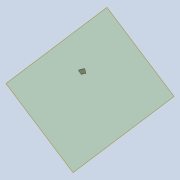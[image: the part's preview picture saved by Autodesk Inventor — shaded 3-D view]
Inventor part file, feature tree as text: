
AUTODESK INVENTOR PART (.ipt)
format: ipt  version: 2020 (Build 240168000, 168)  size: 9,062,912 bytes
history: native  units: in
note: dims shown in document units (in); Inventor stores cm internally (conversion verified against a paired STEP export)
features: other x165, extrude x70, fillet x51, projected_geometry x6, sketch x5, move_body x5, hole x4, loft x3, boolean_combine x2, plane x2, reference x2, direct_edit x1, split x1
ambient origin geometry x8: Origin, YZ Plane, XZ Plane, XY Plane, X Axis, Y Axis, Z Axis, Center Point
bodies: Body (feature_tree), BodyFeature (feature_tree), BodyCut (feature_tree), BodyCutFeature (feature_tree), BodyCutFilletFeature (feature_tree), BodyCutCombineFeature (feature_tree), BodyCutEdgeFilletFeature (feature_tree), BodyRibFrontFilletsFeature (feature_tree), BodyBackRibFilletsFeature (feature_tree), BodyFretboardFilletsFeature (feature_tree), BodyFrontTopFilletsFeature (feature_tree), BodyFrontBottomFilletsFeature (feature_tree), BodyFrontNeckFilletsFeature (feature_tree), Solid22 (feature_tree), Solid23 (feature_tree), Solid62 (feature_tree), Solid64 (feature_tree), Solid65 (feature_tree), Solid68 (feature_tree), Solid50 (feature_tree), Solid52 (feature_tree), Solid54 (feature_tree), Solid56 (feature_tree), Solid57 (feature_tree), Solid59 (feature_tree)
feature tree (317):
  other  "MainBody"
  extrude  "NeckMountsProfileFeature"  Depth=0.5in TaperAngle=0.0deg
  other  "NeckPlane"
  extrude  "8StringFeature"  Depth=4.5in
  extrude  "6StringFeature"  Depth=1.12in
  extrude  "HornFeature"  Depth=0.6788in
  other  "6StringNeckFeature"
  other  "8StringNeckFeature"
  fillet  "InsideCornerFilletsFeature1/8"  Radius=0.6788in
  fillet  "OutsideFilletsFeature1/2"  Radius=0.125in
  fillet  "NeckMountOutsideFilletsFeature1/4"  Radius=0.5in
  fillet  "TipFilletsFeature1/8"  Radius=0.125in
  fillet  "BottomHornTipFilletFeature1/10"  Radius=0.1in
  fillet  "BottomHornFilletsFeature1/8"  Radius=0.125in
  fillet  "InsideHandleFilletsFeature1/2"  Radius=0.5in
  fillet  "InsideHandleFilletsFeature1/8"  Radius=0.125in
  fillet  "InsideTopHornFilletsFeature1/4"  Radius=0.25in
  fillet  "InsideTopHornFilletsFeature1/2"  Radius=0.5in
  fillet  "InsideBottomHornFilletsFeature1/4"  Radius=0.25in
  other  "PickupsOriginal"
  other  "MiddlePlane"
  other  "PickupsCustom"
  other  "PickupsModified"
  extrude  "TopPickupsIndentFeature"  Depth=0.05in
  extrude  "BottomPickupsIndentFeature"  Depth=0.05in
  extrude  "TopPickupHolesFeature"  Depth=0.05in
  extrude  "BottomPickupHolesFeature"  Depth=0.05in
  fillet  "PickupIndentFilletsFeature"  Radius=1.1649in
  other  "Frets"
  other  "FretsPreview"
  other  "TopHornHandleIndent"
  extrude  "TopHornBodyHandleFeature"  Depth=0.05in
  extrude  "TopHornHornHandleFeature"  Depth=0.05in
  other  "HornSculptFeature"
  other  "TopHornHandleFront"
  extrude  "TopHornHandleFrontFeature"  Depth=0.05in
  extrude  "TopHornHandleFront2Feature"  Depth=0.05in
  extrude  "TopHornHandleFront3Feature"  TaperAngle=45.0deg  [1 undecoded]
  other  "TopHornHandleBack"
  extrude  "TopHornHandleBackFeature"  TaperAngle=120.0deg  [1 undecoded]
  extrude  "TopHornHandleBack2Feature"  Depth=0.05in
  extrude  "TopHandleFeature"  Depth=0.05in
  extrude  "TopHandleFrontFeature"  Depth=0.05in
  extrude  "TopHandleBackFeature"  Depth=0.05in
  other  "Tuners"
  hole  "TunerHolesFeature"  [1 undecoded]
  other  "LogoMount"
  extrude  "LogoMountFeature"  Depth=0.05in
  other  "SideProfile"
  extrude  "SideProfileFeature"  Depth=0.05in
  other  "KeyboardCompartmentSidePlane"
  extrude  "KeyboardCompartmentFeature"  Depth=0.05in
  fillet  "KeyboardCompartmentFilletsFeature"  Radius=0.101in
  other  "ControlsBottom"
  other  "ControlsTop2"
  other  "ControlsTop1"
  extrude  "ControlsTop1Feature"  Depth=0.05in
  extrude  "ControlsTop2Feature"  Depth=0.05in
  extrude  "ControlsBottomFeature"  Depth=0.05in
  other  "HornSculptSideProfileFeature"
  fillet  "HornFretboardFilletFeature"  Radius=0.933in
  other  "ElectronicsCompartments"
  other  "InsideFacePlane1"
  other  "InsideFacePlane2"
  other  "InsideFacePlane3"
  extrude  "ElectronicCompartmentTopFeature"  Depth=0.05in
  extrude  "ElectronicCompartmentBottomFeature"  Depth=0.05in
  other  "ElectronicCompartmentsSculpt1Feature"
  other  "ElectronicCompartmentsSculpt2Feature"
  other  "ElectronicCompartmentsSculpt3Feature"
  other  "ElectronicCompartmentsSubtractFeature"
  extrude  "ElectronicCompartmentsSubtract2Feature"  Depth=0.05in
  fillet  "ElectronicCompartmentFillets1Feature"  Radius=3.5in
  fillet  "ElectronicCompartmentFillets2Feature"  Radius=1.277in
  extrude  "ControlIndentsBottomFeature"  Depth=0.05in
  fillet  "ElectronicCompartmentFillets3Feature"  Radius=1.5in
  fillet  "ElectronicCompartmentFillets4Feature"  Radius=1.0857in
  extrude  "ControlIndentsTopFeature"  Depth=0.05in
  other  "ControlIndents2Top"
  extrude  "ControlIndents2TopFeature"  Depth=0.05in
  fillet  "ControlIndents3FilletsFeature"  Radius=4.5in
  extrude  "ControlIndents2RecutFeature"  Depth=0.05in
  fillet  "ElectronicCompartmentInsideFilletsFeature"  Radius=0.1512in
  other  "BottomBridgePickupWirePlane"
  extrude  "BottomBridgePickupWireHoleFeature"  Depth=0.05in
  other  "BottomNeckPickupWirePlane"
  extrude  "BottomNeckPickupWireFeature"  Depth=0.05in
  extrude  "TopPickupWireFeature"  Depth=0.05in
  other  "SeaboardBlockCircuitboardMounts"
  extrude  "SeaboardBlockMountStemFeature"  Depth=0.05in
  extrude  "SeaboardBlockMountsFeature"  Depth=0.05in
  other  "SeaboardBlockKeyMounts"
  extrude  "SeaboardBlockKeyMountsFeature"  Depth=0.05in
  extrude  "SeaboardBlockRibbonsFeature"  Depth=0.05in
  extrude  "TunersTopFeature"  Depth=0.05in
  extrude  "TunersMiddleFeature"  Depth=0.05in
  extrude  "TunersBottomFeature"  Depth=0.05in
  fillet  "TunerFilletsFeature"  Radius=1.1386in
  extrude  "NeckCutFeature"  Depth=0.05in
  fillet  "NeckCutFilletFeature"  Radius=4.009in
  other  "NeckCutCombineFeature"
  fillet  "NeckCutEdgeFilletFeature"  Radius=1.481in
  fillet  "NeckCutCornerFilletsFeature"  Radius=0.25in
  extrude  "NeckMountsFeature"  Depth=0.05in
  extrude  "FretMarkersTopFeature"  Depth=0.05in
  extrude  "FretMarkersBottomFeature"  Depth=0.05in
  extrude  "FretsPreviewFeature"  TaperAngle=0.0deg  [1 undecoded]
  extrude  "FretLocksPreviewFeature"  Depth=0.3937in
  hole  "FretLocksHolesFeature"  [1 undecoded]
  extrude  "TopHornHandleBodyFeature"  Depth=0.05in
  other  "TopHornSculpt3Feature"
  other  "TopHornSculpt4Feature"
  other  "TopHornSculpt5Feature"
  fillet  "TopHornHandleBodyFilletsFeature"  Radius=0.9256in
  fillet  "TopHornHandleFilletsFeature"  [1 undecoded]
  other  "TopHornAdjustFeature"
  fillet  "TopHornAdjustFilletFeature"  [1 undecoded]
  other  "HandlePlane1"
  other  "HandlePlane2"
  other  "Handle"
  extrude  "HandleBackFeature"  Depth=0.05in
  extrude  "HandleFrontFeature"  Depth=0.05in
  other  "HandleSculpt1Feature"
  other  "HandleSculpt2Feature"
  other  "HandleSculpt3Feature"
  other  "HandleSculpt4Feature"
  other  "HandleSculpt5Feature"
  other  "HandleSculpt6Feature"
  other  "HandleEdit1Feature"
  other  "HandleEdit2Feature"
  fillet  "HandleBodyFilletsFeature"  Radius=25.5in
  fillet  "HandleRibFilletsFeature"  Radius=0.3333in
  other  "HornBackSculptFeature"
  other  "HornHandleBackSculpt1Feature"
  other  "HornHandleBackSculpt2Feature"
  fillet  "HornHandleackSculptFilletsFeature"  Radius=0.333in
  fillet  "HandleMeshFilletsFeature"  Radius=0.1in
  fillet  "HornMeshFillets1Feature"  Radius=0.1in
  fillet  "FretboardEndFilletsFeature"  [1 undecoded]
  other  "KeyboardCompartmentSideProfile"
  extrude  "KeyboardCompartmentExactFeature"  Depth=0.05in
  extrude  "KeyboardCompartmentSideFeature"  Depth=0.05in
  other  "KeyboardCompartmentExactSubtractFeature"
  other  "8NeckSplitFeature"
  other  "8NeckLoftStartPlane"
  other  "8NeckLoftEndPlane"
  loft  "8NeckLoftFeature"
  other  "6NeckSplitForLoftFeature"
  other  "6NeckLoftEndPlane"
  other  "6NeckLoftStartPlane"
  extrude  "OscScreenFeature"  TaperAngle=0.0deg  [1 undecoded]
  other  "OscCompartmentPlane"
  other  "OscIndentPlane"
  extrude  "OscCompartmentFeature"  Depth=0.05in
  other  "OscCompartmentSubtractFeature"
  extrude  "OscMountFeature"  Depth=0.05in
  other  "OscCoverIndentPlane"
  extrude  "OscCoverIndentFeature"  Depth=0.05in
  fillet  "OscCoverIndentFilletsFeature"  [1 undecoded]
  extrude  "OscCoverMountHolesFeature"  Depth=0.05in TaperAngle=0.0deg
  fillet  "ElectronicCompartmentLastFilletFeature"  Radius=0.3in
  loft  "6NeckLoftFeature"
  extrude  "6CloseCutFeature"  Depth=0.05in
  other  "HeadSculpt1Feature"
  other  "HeadThickness"
  other  "HeadSculpt2Feature"
  other  "HeadSculpt3Plane"
  extrude  "HeadSculpt3Feature"  Depth=0.05in
  other  "HeadSculpt4Feature"
  other  "8HeadCombineFeature"
  other  "8HeadCleanupFeature"
  fillet  "8HeadFilletFeature"  Radius=0.333in
  other  "HeadSculpt5Plane"
  other  "HeadSculpt5Feature"
  other  "HeadSculpt6Feature"
  other  "HeadSculpt7Plane"
  extrude  "HeadSculpt7Feature"  Depth=0.05in
  other  "6StringCombineFeature"
  other  "6NeckFilletSplitFeature"
  other  "8NeckFilletSplitFeature"
  fillet  "InsideHeadFilletFeature"  Radius=0.125in
  other  "CombineFilletsFeature"
  fillet  "HornHeadFilletsFeature"  Radius=0.5in
  fillet  "HornFillet3Feature"  Radius=5.55in
  other  "HornFinalSplitFeature"
  other  "6FinalSplitFeature"
  other  "6CombineFeature"
  other  "8NeckJoin"
  other  "6NeckJoin"
  extrude  "8NeckJoinFeature"  Depth=0.05in
  fillet  "8NeckJoinFilletFeature"  Radius=0.2in
  extrude  "6NeckJoinFeature"  Depth=0.05in
  extrude  "SeaboardBlockMountHolesFeature"  TaperAngle=0.0deg  [1 undecoded]
  extrude  "PickupRecutFeature"  Depth=0.05in
  extrude  "BackCoverIndentFeature"  Depth=0.3937in
  extrude  "ElectronicsCompartmentSupportFeature"  Depth=0.05in
  fillet  "ElectronicsCompartmentSupportFilletsFeature"  Radius=1.125in
  hole  "BackCoverMountsFeature"  [1 undecoded]
  other  "OscCoverBottom"
  other  "OscCoverTopPlane"
  other  "OscCoverMounts"
  loft  "OscCoverFeature"
  extrude  "OscCoverBodyCutFeature"  Depth=0.05in TaperAngle=0.0deg
  fillet  "OscCoverBodyCutFilletsFeature"  Radius=0.05in
  other  "OscCoverBodyCutSubtractFeature"
  fillet  "OscCoverBodyFilletFeature"  Radius=0.125in
  extrude  "OscCoverMountsFeature"  Depth=0.05in
  other  "LogoCompartment"
  extrude  "LogoCompartmentFeature"  Depth=0.05in
  extrude  "LogoCompartmentMountsFeature"  Depth=0.05in
  fillet  "LogoCompartmentFillet1Feature"  Radius=0.5in
  fillet  "LogoCompartmentFillet2Feature"  Radius=0.25in
  fillet  "LogoCompartmentFillet3Feature"  Radius=0.1in
  fillet  "LogoCompartmentFillet4Feature"  Radius=0.13in
  fillet  "LogoCompartmentFillet5Feature"  Radius=3.063in
  fillet  "LogoCompartmentFillet6Feature"  Radius=0.1295in
  fillet  "LogoCompartmentFillet7Feature"  Radius=0.1295in
  fillet  "LogoCompartmentFillet8Feature"  Radius=0.5708in
  hole  "LogoCompartmentHolesFeature"  [1 undecoded]
  boolean_combine  "Combine26"
  boolean_combine  "Combine27"
  direct_edit  "Direct Edit19"
  plane  "Work Plane97"
  split  "Split16"
  other  "KeyboardCompartment"
  other  "TopHandle"
  other  "TunerLocksBody"
  other  "FretsBody"
  other  "TunersTop"
  other  "TunersMiddle"
  other  "TunersBottom"
  other  "ElectronicCompartments1Body"
  other  "NeckCut"
  other  "NeckMounts"
  other  "TopHornHandle"
  other  "TopHornHandleBody"
  projected_geometry  "Projected Loop22"
  projected_geometry  "Projected Loop23"
  other  "TopHandleFront"
  projected_geometry  "Projected Loop24"
  other  "TopHandleBack"
  other  "HandleBody"
  other  "TopHornSculpt3Plane"
  other  "TopHornSculpt4Plane"
  other  "TopHornSculpt5Plane"
  other  "HandleSculpt1Plane"
  other  "HandleSculpt2Plane"
  other  "HandleSculpt3Plane"
  other  "HandleSculpt4Plane"
  other  "HandleSculpt5Plane"
  other  "HandleSculpt6Plane"
  other  "HornBody"
  other  "8StringBody"
  other  "6StringBody"
  other  "NeckMountsProfile"
  other  "HornBackSculptPlane"
  other  "HornSculptFrontPlane"
  plane  "Work Plane62"
  other  "8NeckStartProfile"
  other  "8NeckEndProfile"
  sketch  "Sketch127"  dims[d8=0.7696in d18=0.5in d119=1.75in d120=0.0in]
  other  "6NeckLoftStartProfile"
  other  "6NeckLoftEndProfile"
  projected_geometry  "Projected Loop27"
  other  "6CloseCut"
  sketch  "Sketch131"  dims[d433=1.0857in d464=4.5in d466=0.25in]
  other  "HeadSculpt1Plane"
  other  "HeadSculpt2Plane"
  other  "HeadSculpt3Profile"
  other  "HeadSculpt4Plane"
  other  "HeadSculpt7Profile"
  other  "6NeckFilletSplit"
  other  "8NeckFilletSplit"
  sketch  "Sketch138"  dims[d501=0.25in d582=1.12in]
  sketch  "Sketch139"  dims[d644=25.0in d654=0.6788in d681=0.6788in d700=0.125in d702=0.5in d703=0.125in d705=0.1in d706=0.125in d707=0.5in d708=0.125in d709=0.25in d710=0.5in d711=0.25in]
  other  "ControlIndentsBottom"
  other  "BottomBridgePickupWireHole"
  other  "BottomNeckPickupWire"
  other  "TopPickupWire"
  other  "HornHandleBackSculpt1Plane"
  other  "HornHandleBackSculpt2Plane"
  sketch  "Sketch165"  dims[d716=2.2835in d717=0.0515in d718=13.825in d719=0.213in d721=0.9414in d722=1.1649in d724=5.7in d725=7.5379in d726=0.2542in d727=2.0in d728=45.0deg d729=120.0deg d730=0.3642in d731=0.9371in d745=5.6289in d747=6.0in d748=4.3in d750=0.8658in d751=0.6506in d753=0.4054in d754=0.8in d779=0.101in d781=1.7in d782=7.125in d783=2.6in d784=0.933in d787=1.1in d792=3.625in d793=4.0in d819=3.5in d825=1.277in d834=1.277in d836=1.5in d837=1.0857in d838=3.0in d839=2.0in d841=4.5in d846=3.3665in d850=0.1512in d853=2.6in d864=1.5757in d961=0.5in d962=0.5in d963=0.3779in d964=0.3779in d965=0.45in d966=0.45in d967=0.8795in d968=1.1386in d969=1.1386in d970=0.45in d971=4.009in d972=1.481in d979=0.25in d980=0.25in d982=0.1718in d983=0.1718in d984=0.0in d985=0.7874in d987=4.0in d988=0.3937in d990=1.0in d994=2.746in d995=1.481in d996=0.9256in d999=0.0in d1000=0.0in d1022=26.75in d1023=28.0in d1024=25.5in d1026=0.3333in d1041=0.333in d1042=0.1in d1044=0.1in d1048=0.0in d1049=0.0in d1054=0.1in d1055=0.1in d1057=0.748in d1060=0.0in d1061=0.0in d1064=0.4662in d1092=0.7in d1095=1.7in d1100=0.0in d1101=0.0in d1117=0.25in d1118=0.0in d1119=0.3in d1120=0.0in d1122=0.2in d1123=0.0in d1277=0.6459in d1329=0.5333in d1334=0.333in d1335=0.5333in d1339=0.125in d1348=0.5in d1358=5.55in d1359=1.75in d1373=0.2in d1375=0.1in d1376=0.0in d1406=1.125in d1430=3.1496in d1432=0.525in d1433=0.3937in d1435=1.0in d1439=1.8in d1440=1.125in d1441=0.2in d1475=0.1in d1476=0.75in d1477=0.375in d1478=0.25in d1479=0.5635in d1480=0.5in d1481=0.8108in d1483=0.05in d1484=0.0in d1485=0.05in d1486=0.0in d1487=0.05in d1488=0.0in d1489=0.125in d1490=0.1in d1491=2.846in d1492=1.481in d1493=0.5in d1494=0.25in d1496=0.1in d1504=0.13in d1508=0.1in d1511=3.063in d1512=0.1295in d1513=0.1295in d1526=0.5708in d1527=0.1286in d1528=1.3799in d1529=1.3958in d1530=1.1055in d1531=0.8208in d1534=2.3622in d1536=0.45in d1537=0.3937in d1539=1.0in d1574=1.0in d1575=0.0in d1576=0.0in d1577=0.4789in d1578=0.4308in d1579=1.1471in d1580=2.5in d1581=1.275in d1582=1.1845in d1583=1.481in d1584=1.1384in d1585=0.7644in d1586=2.746in d1587=0.264in d1588=0.4in d1589=0.0in d1590=0.75in d1591=0.0in d1592=1.0in d1593=0.0in d1594=1.0in d1595=0.0in d1596=0.144in d1597=3.75in d1598=0.1295in d1599=0.1295in d1638=10.0in d1639=14.2465in d1641=11.25in d1648=0.5in d1649=0.0in d1650=28.0in d1657=1.0in d1659=5.5in d1660=4.25in d1662=0.3333in d1663=0.0in d1664=10.0in d1665=1.0in d1671=0.1in d1672=0.5in d1676=3.0in d1677=2.425in d1682=0.75in d1683=0.0in d1690=1.1878in d1691=0.9817in d1692=1.0844in d1693=0.8784in d1695=0.2in d1696=0.0in d1750=1.525in d1751=0.0in d1752=0.5in d1777=0.5in d1778=0.0in d1779=0.5in d1780=0.0in d1781=0.5in d1782=0.0in d1783=0.6in d1784=0.0in d1790=0.65in d1791=0.0in d1792=0.65in d1793=0.0in d1795=0.125in d1821=0.1in d1828=0.0in d1829=0.0in d1830=0.475in d1831=0.125in d1832=0.125in d1843=3.0403in d1844=2.1333in d1845=0.758in d1847=1.75in d1848=0.0in d1849=1.9in d1850=0.0in d1851=1.9in d1852=0.0in d1858=0.9in d1859=0.0in d1862=0.0in d1863=0.0in d1864=0.5in d1865=0.0in d1866=0.5in d1867=0.0in d1870=0.2056in d1871=0.257in d1872=0.0674in d1875=0.25in d1876=0.0in d1877=0.15in d1880=0.15in d1882=0.05in d1883=0.05in d1885=1.3537in d1887=10.0in d1888=0.1in d1889=0.1in d1890=20.0in d1891=20.0in d1894=0.0618in d1900=0.1in d1901=0.4524in d1903=0.006in d1904=0.0in d1915=0.22in d1921=0.0in d1922=90.0deg d1923=0.0in d1924=90.0deg d1925=1.2in d1926=0.7in d1927=0.3333in d1928=0.001in d1929=0.25in d1930=1.25in d1931=0.25in d1935=0.8in d1936=0.3489in d1937=0.22in d1938=0.25in d1939=0.5in d1940=0.6in d1941=0.15in d1942=0.4in d1943=0.0in d1944=90.0deg d1945=0.0in d1946=90.0deg d1948=1.3333in d1949=2.125in d1951=1.125in d1952=2.55in d1957=3.0in d1958=0.1in d1959=0.1in d1960=0.1in d1961=1.0in d1962=0.0in d1966=1.0in d1967=0.0in d1968=0.44in d1969=0.0in d1975=0.1in d1976=0.1in d1980=10.6875in d1981=5.1875in d1982=0.85in d1983=0.3333in d1985=7.5816in d1987=0.1in d1988=0.0in d1989=0.1875in d1990=0.5333in d1992=150.0deg d1993=3.25in d1996=-0.325in d1997=-0.125in d1998=1.0in d1999=0.0in d2004=0.5in d2005=0.0in d2007=0.0938in d2008=0.5in d2009=0.25in d2010=2.3125in d2011=0.7188in d2015=0.25in d2016=5.0in d2019=0.125in d2020=0.25in d2027=0.2in d2028=0.0in d2029=0.02in d2030=0.0in d2039=0.55in d2047=0.25in d2048=0.25in d2049=0.0in d2050=0.0in d2052=2.295in d2053=0.0in d2056=0.25in d2058=0.25in d2059=0.3333in d2060=0.3333in d2061=0.25in d2062=0.3333in d2063=0.3333in d2064=0.0in d2065=0.0in d2066=0.339in d2067=0.1643in d2068=0.1in d2069=0.1in d2070=0.1in d2071=0.1in d2072=0.1643in d2073=0.1643in d2074=0.1643in d2077=3.3125in d2078=3.313in d2079=0.305in d2080=0.3333in d2081=1.0in d2082=0.0in d2083=0.3333in d2084=0.0in d2086=0.719in d2087=2.3125in d2088=0.125in d2089=0.1in d2090=0.438in d2091=0.438in d2092=0.438in d2093=0.438in d2094=0.25in d2095=0.0in d2096=0.25in d2097=0.25in d2098=2.0in d2100=2.5in d2102=0.75in d2103=0.25in d2104=0.25in d2105=0.0in d2106=0.625in d2111=10.0in d2112=0.125in d2113=0.3333in d2117=1.75in d2118=1.25in d2119=1.625in d2120=0.25in d2121=1.0in d2122=0.1in d2125=0.7in d2132=1.625in d2133=1.0in d2134=0.1in d2135=1.0in d2136=1.0in d2137=0.1in d2138=1.025in d2139=1.025in d2140=0.5in d2141=0.7in d2142=1.075in d2143=0.7in d2144=0.5in d2146=0.25in d2147=0.25in d2148=0.5in d2149=1.75in d2150=0.0in d2151=0.0in d2152=0.035in d2153=0.0in d2154=0.0in d2155=0.0in d2156=-0.325in d2157=1.0in d2158=0.2in d2159=0.0in d2160=1.0in d2161=0.2in d2162=0.0in d2164=1.0in d2165=2.2612in d2166=0.605in d2167=0.01in d2168=0.3333in d2169=0.5388in d2170=0.4in d2171=2.625in d2172=1.375in d2173=0.172in d2174=0.281in d2175=0.5in d2176=0.0in d2177=-2.0in d2178=1.797in d2179=0.0in d2180=-0.125in d2181=0.06in d2182=0.06in d2183=0.505in d2184=0.9375in d2185=2.625in d2186=1.375in d2187=2.5in d2188=1.0313in d2189=0.05in d2190=0.1719in d2191=0.0625in d2192=0.0625in d2193=0.1094in d2194=0.0312in d2195=0.0312in d2196=0.0312in d2197=0.0312in d2198=0.0312in d2199=0.0312in d2200=0.0312in d2201=0.0312in d2202=0.203in d2203=0.0in d2207=-0.2in d2211=0.15in d2212=1.0in d2213=0.0in d2214=0.15in d2215=0.15in d2216=0.1in d2220=0.05in d2221=1.5in d2222=0.0in d2230=0.6836in d2238=1.0in d2239=0.25in d2240=0.1in d2241=0.0689in d2243=1.1408in d2244=0.449in d2245=1.6223in d2246=2.1038in d2247=0.449in d2248=0.0463in d2249=0.4549in d2251=0.3908in d2252=0.3908in d2255=0.8in d2257=3.5in d2259=1.1973in d2261=0.625in d2262=0.625in d2263=0.536in d2264=2.7in d2265=0.25in d2266=0.2in d2267=0.0in d2268=0.2in d2269=0.0in d2278=0.4264in d2279=1.0in d2280=0.0in d2281=21.986in d2282=0.0in d2283=0.1in d2284=0.1in d2285=0.5in d2286=0.0in d2287=0.5333in d2288=0.1in d2293=0.85in d2294=1.0in d2295=0.25in d2296=0.749in d2297=0.0in d2298=0.25in d2299=0.1984in d2300=0.1in d2301=0.0in d2302=0.2in d2303=0.0in d2304=0.481in d2305=0.481in d2306=0.5in d2307=0.25in d2308=0.1in d2309=0.75in d2310=0.375in d2311=0.25in d2312=0.5635in d2313=0.5in d2314=0.8108in d2319=0.0in d2320=0.0in d2321=90.0deg d2322=0.0in d2323=90.0deg d2324=0.5in d2325=0.0in d2326=28.0in d2327=1.0in d2328=1.5in d2329=0.0in d2330=0.2in d2331=0.2in d2333=0.22in d2335=0.12in d2336=0.12in d2337=0.1in d2338=0.1in d2339=0.75in d2340=0.375in d2341=0.25in d2342=0.5635in d2343=0.5in d2344=0.8108in d2347=0.25in d2348=0.3in d2349=0.15in d2350=0.15in d2351=0.3in d2352=0.15in d2353=0.3in d2354=0.25in d2355=0.25in d2356=0.25in d2357=0.25in d2358=0.25in d2359=0.1958in d2360=0.1958in d2365=0.2in d2366=0.0in d2381=0.7in d2382=0.6in d2387=0.089in d2408=0.3333in d2409=0.0in d2410=0.031in d2412=0.106in d2413=0.072in d2414=0.033in d2415=0.125in d2416=0.132in d2417=0.101in d2418=0.074in d2419=0.05in d2420=0.75in d2421=0.375in d2422=0.25in d2423=0.5635in d2424=0.5in d2425=0.8108in d2428=0.0in d2429=0.0in d2430=-0.0394in d2431=0.0in d2432=0.0in d2433=-0.0394in d2434=0.0in d2435=0.0in d2436=-0.0394in d2437=0.0in d2438=0.0in d2439=-0.0394in d620=0.5in d621=0.0344in d622=0.5in d623=0.0344in d1625=0.5in d1626=0.0344in d1627=0.5in d1628=0.0344in d1730=0.5in d1731=0.0344in d1732=0.5in d1733=0.0344in d1822=0.5in d1823=0.0344in d1824=0.5in d1825=0.0344in d1837=0.5in d1838=0.0344in d1839=0.5in d1840=0.0344in d1860=0.5in d1861=0.0344in d1947=0.5in d1950=0.0344in d2012=0.5in d2013=0.0344in d2101=0.5in d2392=0.5in d2393=0.0344in d2394=0.5in d2395=0.0344in]
  other  "OscScreen"
  other  "OscCompartment"
  other  "OscMount"
  other  "OscCoverPlane"
  other  "OscCoverIndent"
  other  "OscCoverMountHoles"
  projected_geometry  "Projected Loop32"
  other  "KeyboardCompartmentExact"
  projected_geometry  "Projected Loop35"
  other  "SeaboardBlockMountHoles"
  reference  "Reference6"
  reference  "Reference7"
  other  "PickupRecut"
  other  "BackCoverIndent"
  other  "ElectronicsCompartmentSupport"
  other  "BackCoverMounts"
  other  "OscCoverTop"
  other  "OscCoverBody"
  other  "Delete13"
  move_body  "Move3"
  other  "Delete14"
  other  "6StringNeckCombineBody"
  other  "8StringNeckBody"
  other  "6StringNeckBody"
  other  "TopHornBody"
  other  "8StringCombinedBody"
  other  "6StringCombinedBody"
  other  "Delete18"
  other  "<userpath>\Desktop\switchback\src\switchback-exploded.iam"
  other  "switchback-exploded.iam"
  other  "seaboard-block-keyboard:1"
  move_body  "Move4"
  move_body  "Move5"
  move_body  "Move6"
  move_body  "Move7"
note: 13 required parameter values undecoded (feature->parameter linkage not recoverable at this tier; creation-order binding heuristic only, values carry confidence <= 0.55)
